# Revit family: R0000103
name_source: partatom
category: Türen
units: mm (PartAtom-declared; Revit-internal decimal feet)

## family parameters
Basisbauteil = Wand
Beim Laden mit Abzugskörper schneiden = Nein
Gemeinsam genutzt = Nein
Immer vertikal = Ja
Raumberechnungspunkt = Ja

## types (1)
- BOS SvdW-D für Mauerwerk mit NOVA 150 BOS Holz
    1-Kammer-Dichtung = Nein
    Anschlagprofilbreite = 95 mm
    Aufdopplung = Ja
    Aufdopplungstiefe = 3 mm  [stored 0.00984252 ft]
    BE max. = 100 mm  [stored 0.328084 ft]
    Bauelement = BOS Stahlzarge
    Beschreibung = Schiebetürzarge für vor der Wand laufende Schiebetüren (LineaOutside-D) für Mauerwerk
    Breite = 0 mm  [stored 0 ft]
    Dichtungsprofil 16 mm = Ja
    Dicke = 0 mm  [stored 0 ft]
    Dornmaß = 65 mm  [stored 0.213255 ft]
    Einfügepunkt = 37 mm  [stored 0.121391 ft]
    Fingerschutz-Abstand = 51 mm
    Funktion = Innen
    Führungsnutbreite = 18 mm  [stored 0.0590551 ft]
    Führungsnuttiefe = 36 mm  [stored 0.11811 ft]
    Griffhöhe = 1068 mm  [stored 3.50394 ft]
    Grifflänge = 800 mm  [stored 2.62467 ft]
    Griffradius = 9 mm  [stored 0.0295276 ft]
    Grifftiefe = 46 mm  [stored 0.150919 ft]
    Hersteller = BOS GmbH Best Of Steel, Lütkenfelde 4, D-48282 Emsdetten
    Info-Texte sichtbar = Ja
    Information in English = Nein
    LDB max. = 1186 mm  [stored 3.89108 ft]
    LDB min. = 561 mm
    LDH max. = 2218 mm  [stored 7.2769 ft]
    LDH min. = 1843 mm  [stored 6.04659 ft]
    MW max. = 560 mm  [stored 1.83727 ft]
    MW min. = 100 mm  [stored 0.328084 ft]
    Material = grundiert, feuerverzinktes Feinblech nach DIN EN 10143
    Material - Dichtung = <Nach Kategorie>
    Material - Führungszapfen = <Nach Kategorie>
    Material - Laufschiene = <Nach Kategorie>
    Material - Türblatt = <Nach Kategorie>
    Material - Türgriff = <Nach Kategorie>
    Material - Zarge = <Nach Kategorie>
    Modell = SvdW-D mit NOVA 150 BOS Holz
    NOVA 150 BOS Holz = Ja
    Putzwinkel hinten max. = 28 mm  [stored 0.0918635 ft]
    Putzwinkel hinten min. = 9 mm  [stored 0.0295276 ft]
    Putzwinkel vorne AP = 15 mm  [stored 0.0492126 ft]
    Putzwinkel vorne KS = 17 mm  [stored 0.0557743 ft]
    Putzwinkel vorne STL = 14 mm  [stored 0.0459318 ft]
    Putzwinkel vorne STR = 17 mm  [stored 0.0557743 ft]
    Rohbaubreite = 0 mm  [stored 0 ft]
    Rohbauhöhe = 0 mm  [stored 0 ft]
    Spiegel hinten max. = 80 mm  [stored 0.262467 ft]
    Spiegel hinten min. = 30 mm  [stored 0.0984252 ft]
    Stoßgriff = Ja
    SvdW-D mit NOVA 150 BOS Holz = Ja
    TB = 1
    Technische Infos rund um die Stahlzarge = www.BestOfSteel.de/tools-downloads/technische-infos-rund-um-die-stahlzarge/
    Türblattstärke = 40 mm  [stored 0.131234 ft]
    URL = www.BestOfSteel.de/stahlzargen/zargen-fuer-schiebetueren/lineaoutside/lineaoutside-d
    Zargenblechstärke = 1.5 mm  [stored 0.00492126 ft]

note: [stored X ft] marks values corroborated as IEEE doubles in the binary element streams (Revit-internal decimal feet)

## geometry (parser evidence)
native form markers: Extrusion x8
no freeform markers — native parametric forms only
